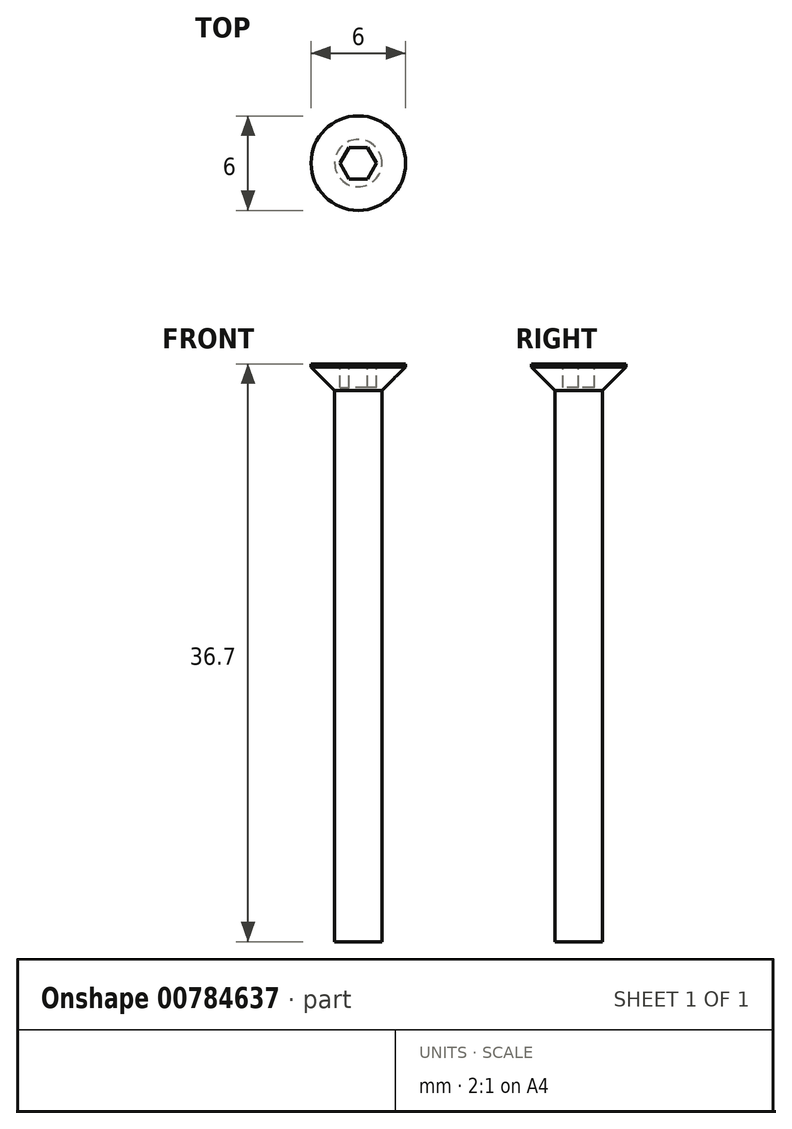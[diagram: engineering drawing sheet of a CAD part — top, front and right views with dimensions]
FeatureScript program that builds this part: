
annotation { "Feature Type Name" : "Feature", "Feature Type Description" : "" }
export const myFeature = defineFeature(function(context is Context, id is Id, definition is map)
    precondition{}
    {
        {
            var Q0;
            Q0=qCreatedBy(makeId("Top.planeOp"),FACE);
            var sketch = newSketch(context, id + "F0", { "sketchPlane" : qUnion([Q0])});
            skCircle(sketch, "E0", {"center": v(0, 0) * mm, "radius": 3 * mm});
            skCircle(sketch, "E1", {"center": v(0, 0) * mm, "radius": 1.5 * mm});
            skSolve(sketch);
        }
        {
            var Q0;
            Q0=makeQuery(id+"F0.imprint","IMPRINT",FACE,{"disambiguationData":[TD([[makeQuery(id+"F0.imprint","IMPRINT",EDGE,{"derivedFrom":sQuery(id+"F0.wireOp",EDGE,"E1")}),1.0]])]});
            extrude(context, id + "F1", {"entities" : qUnion([Q0]), "oppositeDirection" : true, "depth" : 35 * mm, "offsetDistance" : 25 * mm});
        }
        {
            var Q0;
            Q0=makeQuery(id+"F0.imprint","IMPRINT",FACE,{"disambiguationData":[TD([[makeQuery(id+"F0.imprint","IMPRINT",EDGE,{"derivedFrom":sQuery(id+"F0.wireOp",EDGE,"E0")}),1.0]])]});
            var Q1;
            Q1=makeQuery(id+"F0.imprint","IMPRINT",FACE,{"disambiguationData":[TD([[makeQuery(id+"F0.imprint","IMPRINT",EDGE,{"derivedFrom":sQuery(id+"F0.wireOp",EDGE,"E1")}),1.0]])]});
            extrude(context, id + "F2", {"entities" : qUnion([Q0, Q1]), "operationType" : NewBodyOperationType.ADD, "depth" : 1.7 * mm, "offsetDistance" : 25 * mm});
        }
        {
            var Q0;
            Q0=makeQuery(id+"F2.opExtrude","CAP_FACE",FACE,{"disambiguationData":[OSD([sQuery(id+"F0.wireOp",EDGE,"E0")])],"isStart":false});
            var sketch = newSketch(context, id + "F3", { "sketchPlane" : qUnion([Q0])});
            skCircle(sketch, "E2.cCircle", {"center": v(0, 0) * mm, "radius": 1 * mm, "construction": true});
            skLineSegment(sketch, "E2.0", {"start": v(0.58, -1) * mm, "end": v(-0.58, -1) * mm});
            skLineSegment(sketch, "E2.1", {"start": v(-0.58, -1) * mm, "end": v(-1.15, 0) * mm});
            skLineSegment(sketch, "E2.2", {"start": v(-1.15, 0) * mm, "end": v(-0.58, 1) * mm});
            skLineSegment(sketch, "E2.3", {"start": v(-0.58, 1) * mm, "end": v(0.58, 1) * mm});
            skLineSegment(sketch, "E2.4", {"start": v(0.58, 1) * mm, "end": v(1.15, 0) * mm});
            skLineSegment(sketch, "E2.5", {"start": v(1.15, 0) * mm, "end": v(0.58, -1) * mm});
            skPoint(sketch, "E2.0.midPoint", {"position": v(0, -1) * mm});
            skSolve(sketch);
        }
        {
            var Q0;
            Q0=makeQuery(id+"F3.imprint","IMPRINT",FACE,{"disambiguationData":[TD([[makeQuery(id+"F3.imprint","IMPRINT",EDGE,{"derivedFrom":sQuery(id+"F3.wireOp",EDGE,"E2.0")}),-1.0]])]});
            extrude(context, id + "F4", {"entities" : qUnion([Q0]), "operationType" : NewBodyOperationType.REMOVE, "oppositeDirection" : true, "depth" : 1.5 * mm, "offsetDistance" : 25 * mm});
        }
        {
            var Q0;
            Q0=makeQuery(id+"F2.opExtrude","CAP_EDGE",EDGE,{"disambiguationData":[OSD([sQuery(id+"F0.wireOp",EDGE,"E0")])],"isStart":true});
            chamfer(context, id + "F5", {"entities" : qUnion([Q0]), "width" : 1.5 * mm, "tangentPropagation" : true});
        }
    });
